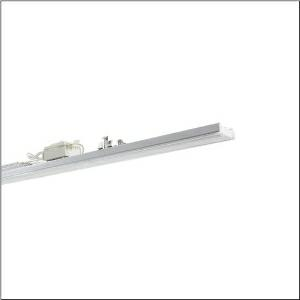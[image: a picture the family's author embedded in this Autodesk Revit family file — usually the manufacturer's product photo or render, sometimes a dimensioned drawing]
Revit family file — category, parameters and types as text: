
# Revit family: licross_21_recessed_ho_52te12cn4c5m
name_source: partatom
category: Lighting Fixtures
units: mm (PartAtom-declared; Revit-internal decimal feet)

## family parameters
Cut with Voids When Loaded = No
Host = Face
Light Source = No
Part Type = Normal
Room Calculation Point = No
Round Connector Dimension = Use Diameter
Shared = No

## types (1)
- --- (1 x LED, 12670 lm, 68.4 W, 4000K)
    Apparent Load = 68 VA
    CIE Flux Codes = 69 91 98 100 100
    Color Rendering = 80
    Color Temperature = 4000K
    Default Elevation = 1800 mm
    Description = Licross 21 Recessed HO, luminaire insert, of sheet steel, galvanised, coil coated, white, length: 1.500mm, width: 66mm, height: 67mm, LED rated luminous flux: 12.670lm, light colour: 840, SDCM (Standard Deviation of Colour Matching)MacAdam ≤ 3 SDCM (initial), control gear: ON/OFF Multilumen, CLOi, with plug, 3-pole, with phase selection, mains connection: 220..240V, AC, 50/60Hz, start of lifetime: 68W, end of service life: 83W, internal wiring halogen-free, primary optical cover: cover, of PMMA, light emission: direct distribution, primary light characteristic: symmetric, protection rating (complete): IP54, insulation class (complete): insulation class I (protective earthing), certification: CE, ENEC, VDE, UKCA, protection symbol: D if used in an environment with non-conductive dust loads with corresponding accessories, impact resistance: IK06, permissible ambient temperature for indoor applications: -35..+30°C, corresponds to IFS (International Featured Standards) requirements for safety and quality in the food industry, reducing of maximum allowable ambient temperature of 5°C with ceiling mounting, LABS conformity tested according to VDMA 24364:2018-05, The light source and the operating device comply with the requirements of the Ecodesign Regulation (EU) 2019/2020 and are replaceable in accordance with this regulation, packaging unit: 1 piece
    Height = 58 mm
    Lamp = 1 x LED
    Lamp Light Flux = 12670 lm
    Lamp Power = 68.4 W
    Lamp count = 1
    Length = 1500 mm
    Luminous efficacy = 185 lm/W
    Manufacturer = Siteco
    ModVariant = No
    Model = 52TE12CN4C5M
    Mounting Place = Ceiling
    Mounting Type = Pendant
    Number of Poles = 1
    OnlyDefault = Yes
    Power Factor = 1
    Product Name = Licross 21 Recessed HO
    Product group = luminaire insert | ceiling pendant
    ProductGroupID = 901
    Protection Class = Protection class I
    Protection Degree = IP 54
    RLX_Detail_Level = 1
    RLX_Emergency_Light_Flux = 0 lm
    RLX_Emergency_Type = 0
    RLX_Emergency_Type_DB = No
    RlxData = <blob elided: 22633 chars, md5=125931e0>
    Socket = socket
    Standby Power = 0 W
    System Light Flux = 12670 lm
    System Power = 68 W
    Type Comments = factory setting: luminous flux: 100 % | (A | C | E) | 161 mA
    Type Image = l_1296930.jpg
    URL = http://relux.com
    VarID = @adj_109745
    Voltage = 0 V
    Weight = 0.00 kg
    Width = 66 mm

## geometry (parser evidence)
native form markers: Blend x4, Sweep x10
no freeform markers — native parametric forms only
